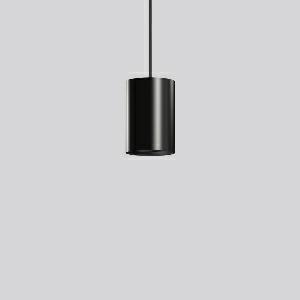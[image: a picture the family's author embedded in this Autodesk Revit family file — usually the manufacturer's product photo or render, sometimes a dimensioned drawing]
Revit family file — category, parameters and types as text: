
# Revit family: deecos_p_maxi_911534_003_1_7632
name_source: partatom
category: Lighting Fixtures
units: mm (PartAtom-declared; Revit-internal decimal feet)

## family parameters
Cut with Voids When Loaded = No
Host = Face
Light Source = No
Part Type = Normal
Room Calculation Point = No
Round Connector Dimension = Use Diameter
Shared = No

## types (1)
- DEECOS P maxi (1 x LED Modul 940, 2850 lm, 4000)
    Apparent Load = 25 VA
    Approval mark = CE
    CIE Flux Codes = 96 100 100 100 100
    Color Rendering = 92
    Color Temperature = 4000
    Default Elevation = 1800 mm
    Description = Series: DEECOS P maxi
Cylindrical pendant luminaire. Housing: die-cast aluminium, powder-coated. Canopy made of powder-coated sheet steel with magnetic attachment. Optical assembly with lens made of plastic (polycarbonate) for the best homogeneous light distribution - can be changed without tools. Best colour rendering index Ra>90. Transparent suspension cable 2 m, can be shortened. High quality converter without flickering and stroboscopic effect. The following accessories can be mounted without use of tools: interchangeable lenses, honeycomb louvre, clear and frosted diffusers, white interchangeable plastic ring. Decorative recessed suspension set available as accessory. 
Colour: deep black, matt (RAL 9005)
Diameter: 123 mm
Height: 181 mm
Suspension length: 2000 mm
Lamp: LED
Socket: without socket
Colour temperature: 4000K
Colour rendering index (CRI): 92
System power: 25 W
Rated luminous flux: 2850 lm
Luminous efficiency: 114 lm/W
Control gear: Regulated power supply
Protection class: I
Type of protection: IP 20
    Height = 181 mm
    Lamp = 1 x LED Modul 940
    Lamp Light Flux = 2850 lm
    Lamp count = 1
    Length = 123 mm
    Lifetime = 50000 h
    Luminous efficacy = 114 lm/W
    Manufacturer = RZB
    ModVariant = No
    Model = 911534.003.1
    Mounting Place = Ceiling
    Mounting Type = Pendant
    Number of Poles = 1
    OnlyDefault = Yes
    Power Factor = 1
    Product Name = DEECOS P maxi
    Product group = Pendant luminaires
    ProductGroupID = 902
    Protection Class = Protection class I
    Protection Degree = IP 20
    RLX_Detail_Level = 1
    RLX_Emergency_Light_Flux = 0 lm
    RLX_Emergency_Type = 0
    RLX_Emergency_Type_DB = No
    RlxData = <blob elided: 36565 chars, md5=0df21b4d>
    Socket = socket
    Standby Power = 0 W
    System Light Flux = 2850 lm
    System Power = 25 W
    Type Comments = Product without accessories
    Type Image = 911480.003.jpg
    URL = http://relux.com
    VarID = ---
    Voltage = 230 V
    Voltage Range = 220-240 V
    Weight = 0.00 kg
    Width = 0 mm  [stored 0 ft]

note: [stored X ft] marks values corroborated as IEEE doubles in the binary element streams (Revit-internal decimal feet)

## geometry (parser evidence)
native form markers: Blend x4, Sweep x10
no freeform markers — native parametric forms only
